# Revit family: 3f_filippi_-_3f_cub_sp_3f_filippi_-_56344_-_3f_cub_led_100w_cr_sp
name_source: partatom
category: Lighting Fixtures
units: mm (PartAtom-declared; Revit-internal decimal feet)

## family parameters
Cut with Voids When Loaded = No
Host = Face
Light Source = No
Part Type = Normal
Room Calculation Point = No
Round Connector Dimension = Use Diameter
Shared = No

## types (1)
- 3F Filippi - 3F Cub SP (1 x LED, 14323 lm, 108 W, 4000 K)
    Apparent Load = 108 VA
    Approval mark = CE
    CIE Flux Codes = 60 89 98 100 100
    Color Rendering = 80
    Color Temperature = 4000 K
    Control Gear = Electronic ballast
    Default Elevation = 1800 mm
    Description = ILLUMINOTECHNICAL
Luminous efficiency 100% (DLOR 100%, ULOR 0%).
Initial luminous flux of the luminaire 14323 lm.
Symmetric wide direct distribution.
Installation Interdistance Transv.D = 1.05 x hu - Long.D = 1.27 x hu.
Tabular UGR (CIE 117 - 4H-8H; S=0.25H; 70/50/20): RUG 22.5 - 22.8.
Beam angle: 88° - 95°.
Luminous efficacy 133 lm/W.
Lifetime (L90/B10): 30000 h. (tq+25°C)
Lifetime (L85/B10): 50000 h. (tq+25°C)
Lifetime (L80/B20): 80000 h. (tq+25°C)
Lifetime (L70/B20): 100000 h. (tq+25°C)
Lifetime (L70/B10): 50000 h. (tq+45°C)
Sudden decreased luminous flux after 50000 hours: 0% (C0).
Photobiological safety in compliance with IEC/TR 62778: RG0 risk exempt, (IEC 62471).
In compliance with IEC/EN 62722-2-1 - IEC/EN 62717 standards.

SOURCE
4 linear LED modules 25W/840.
Energy efficiency class (UE 2019/2020 - UE 2019/2015): C.
CIE 13.3 Colour rendering index: CRI >80 (R9 <50%).
IES TM-30 Fidelity Index: Rf = 84 Rg = 95.
CCT nominal colour temperature 4000 K.
Colour initial tolerance (MacAdam): SDCM 3.

MECHANICAL
Housing with double casing in pressed aluminium, powder-coated in white epoxy-polyester, hinged opening.
Quick connection in polycarbonate M20x1.5 cable gland for access to the terminal block.
Ecologic anti-aging injected sealing gasket.
Stainless steel clips.
Total flow recuperator in specular aluminium, with superficial titanium-magnesium treatment, non-iridescent.
Prismatic flat diffuser in multilenticular methacrylate (PMMA), anti-glare, prismatic outer surface, does not yellow or age.
Fixing bracket for busbar or suspension in galvanised steel.
Luminaire with limited surface temperature. - D - (EN 60598-2-24)
Dimensions: 680x680 mm, height 187 mm. Weight 9.025 kg.
IP64 protection degree.
Mechanical strength to impacts IK08 (5 joule).
Glow-wire test resistance 650°C.

ELECTRICAL
Halogen Free electronic wiring 230V-50/60Hz, power factor 0.95, THD <25%, constant output current, class I, 2 driver.
Twin-circuit.
Power of the luminaire 108 W.
ENEC - CE.
SAFE FLICKER: PstLM=<1 and SVM=<0.4 (IEC TR 61547-1 and IEC TR 63158), to ensure a more comfortable and safe light.
Luminaire compliant with EN 60598-2-22 for power supply from a centralised emergency system CPSS (Central Power Supply System), not incorporated in the luminaire - high risk areas excluded. The default power and flux are 100% in AC and 100% in DC.
Ambient temperature from -20°C to +45°C.
Temperature class T6 max 85°C.
Quick connection.
Relative humidity UR: <85%.

INSTALLATION
Ceiling / Suspended.
All accessories dedicated to this product are available on the Catalog and on our website www.3F-Filippi.com.

APPLICATIONS
Suitable product for food production plants (HACCP), IFS (Food Version 6), BRC (GSFS Food Version 7).
In commercial environments, exhibition and industrial areas, stores, open areas.

WARNING
Fixture not suitable for cold stores with an ambient temperature <0°C and/or relative humidity >85%.
Luminaire designed for disposal/recycling at end-of-life.
Replaceable (LED only) light source by a professional. Replaceable control gear by a professional.
    Height = 187 mm
    Lamp = 1 x LED
    Lamp Light Flux = 14323 lm
    Lamp Power = 108 W
    Lamp count = 1
    Length = 680 mm
    Lifetime = 50000 h
    Luminous efficacy = 133 lm/W
    Manufacturer = 3F Filippi
    ModVariant = No
    Model = 3F Filippi - 56344 - 3F CUB LED 100W CR SP
    Mounting Place = Ceiling
    Mounting Type = Pendant
    Number of Poles = 1
    OnlyDefault = Yes
    Power Factor = 1
    Product Name = 3F Filippi - 3F Cub SP
    Product group = pendant luminaire
    ProductGroupID = 9
    Protection Class = Protection class I
    Protection Degree = IP 64
    RLX_Detail_Level = 1
    RLX_Emergency_Light_Flux = 0 lm
    RLX_Emergency_Type = 0
    RLX_Emergency_Type_DB = No
    RlxData = <blob elided: 44301 chars, md5=f1c19438>
    Socket = socket
    Standby Power = 0 W
    System Light Flux = 14323 lm
    System Power = 108 W
    Type Comments = Product without accessories
    Type Image = 3ffilippi_56344.jpg
    URL = http://relux.com
    VarID = ---
    Voltage = 0 V
    Weight = 0.00 kg
    Width = 680 mm

## geometry (parser evidence)
native form markers: Sweep x9
no freeform markers — native parametric forms only
